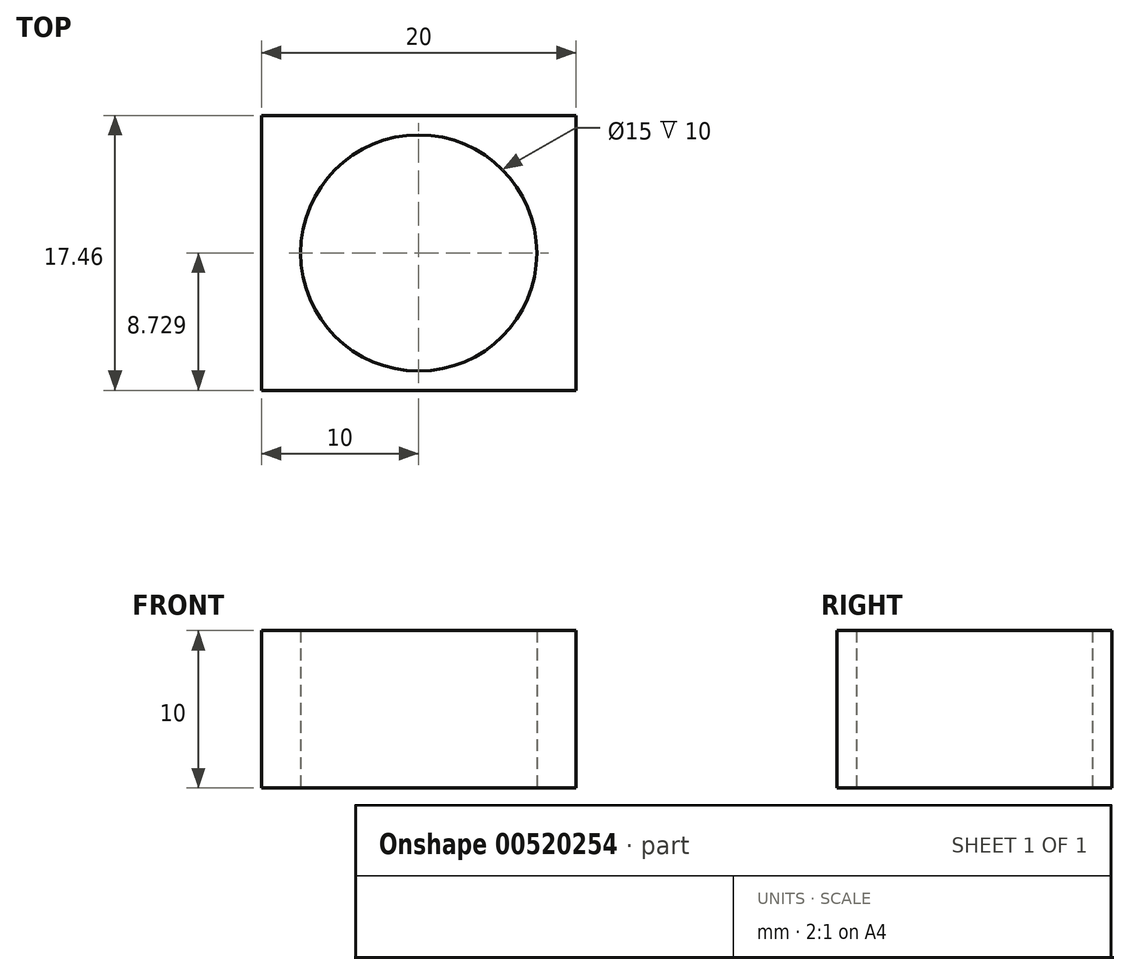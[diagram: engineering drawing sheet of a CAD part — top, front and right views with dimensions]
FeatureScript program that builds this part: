
annotation { "Feature Type Name" : "Feature", "Feature Type Description" : "" }
export const myFeature = defineFeature(function(context is Context, id is Id, definition is map)
    precondition{}
    {
        {
            var Q0;
            Q0=qCreatedBy(makeId("Top.planeOp"),FACE);
            var sketch = newSketch(context, id + "F0", { "sketchPlane" : qUnion([Q0])});
            skLineSegment(sketch, "E0.bottom", {"start": v(-50.08, 41.3) * mm, "end": v(-70.08, 41.3) * mm});
            skLineSegment(sketch, "E0.top", {"start": v(-50.08, 58.76) * mm, "end": v(-70.08, 58.76) * mm});
            skLineSegment(sketch, "E0.left", {"start": v(-50.08, 41.3) * mm, "end": v(-50.08, 58.76) * mm});
            skLineSegment(sketch, "E0.right", {"start": v(-70.08, 41.3) * mm, "end": v(-70.08, 58.76) * mm});
            skPoint(sketch, "E0.middle", {"position": v(-60.08, 50.03) * mm});
            skCircle(sketch, "E1", {"center": v(-60.08, 50.03) * mm, "radius": 7.5 * mm});
            skSolve(sketch);
        }
        {
            var Q0;
            Q0=makeQuery(id+"F0.imprint","IMPRINT",FACE,{"disambiguationData":[TD([[makeQuery(id+"F0.imprint","IMPRINT",EDGE,{"derivedFrom":sQuery(id+"F0.wireOp",EDGE,"E0.bottom")}),-1.0]])]});
            extrude(context, id + "F1", {"entities" : qUnion([Q0]), "depth" : 10 * mm, "offsetDistance" : 25 * mm});
        }
    });
